# Revit family: Холодильные шкафы специализированные
name_source: partatom
category: Оборудование
units: mm (PartAtom-declared; Revit-internal decimal feet)

## family parameters
Всегда вертикально = Да
Классификация = Нет
На основе рабочей плоскости = Нет
Общий = Нет
При загрузке вырезать с полостями = Нет
Размер круглого соединителя = Использовать диаметр
Тип детали = Нормальный
Точка расчета площади = Нет

## types (5) — shared parameters
UV-лампа = +
Высота = 1960 мм
Габаритные размеры, мм = 697*1005*1960
Глубина = 1005 мм
Диап. рабочих темп. = -2....+30
Мат. обшивок корпуса изнутри = нерж. сталь
Мат. обшивок корпуса снаружи = нерж. сталь (кроме задней стенки)
Объем, л = 700
Педаль = +
Потребляемая мощность, Вт = 550/900
Размеры в упаковке, мм = 790x1080x2125
Расположение агрегата = верхнее
Расход электроэнергии за сутки, кВт/ч = 8
Регул. уровня влажности, % = от 60 до 95
Система электропитания, В/Гц = 230/50
Темп. окр. среды = до +40
Хладагент = R134a
Холодильный шкаф = <По категории>
Ширина = 697 мм
zero-valued in all types: Отметка по умолчанию

## per-type parameters (varying)
| type | Вес нетто/брутто, кг | Клапан Шредера | Тип 1 комплектация | Тип оттайки | Тип охлаждения | Цена, руб. |
| CS107-Salami | 130/155 |  | 3 пары направляющих с тремя перекладинами и подвесами |  |  | 205 300 |
| CS107-Cheese Тип 1 | 125/150 | + | 4 сетчатый полки из стали с п/покрытием | автомат. с системой исп. конденсата | динамический с мягким обудвом без заветривания | 202 700 |
| CS107-Cheese Тип 2 | 125/150 | + | 4 перфорированные полки из нерж. стали | автомат. с системой исп. конденсата | динамический с мягким обудвом без заветривания | 205 700 |
| CS107-Meat Тип 1 | 130/155 | + | Штанга + 2 сетчатые полки из стали с п/покрытием | автомат. с системой исп. конденсата | динамический с мягким обудвом без заветривания | 205 380 |
| CS107-Meat Тип 2 | 130/155 | + | 4 перфорированные полки из нержавеющей стали | автомат. с системой исп. конденсата | динамический с мягким обудвом без заветривания | 206 600 |
